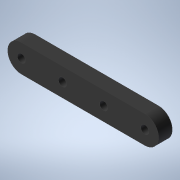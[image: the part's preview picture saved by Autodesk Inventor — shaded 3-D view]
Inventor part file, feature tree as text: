
AUTODESK INVENTOR PART (.ipt)
format: ipt  version: 2020.2 (Build 242310000, 310)  size: 146,432 bytes
history: native  units: mm
features: other x1, sketch x1, extrude x1, hole x1
ambient origin geometry x8: Origin, YZ Plane, XZ Plane, XY Plane, X Axis, Y Axis, Z Axis, Center Point
bodies: Body1 (feature_tree)
feature tree (4):
  other  "ソリッド1"
  sketch  "スケッチ1"
  extrude  "押し出し1"  Depth=10.0mm
  hole  "穴1"  [1 undecoded]
note: 1 required parameter value undecoded (feature->parameter linkage not recoverable at this tier; creation-order binding heuristic only, values carry confidence <= 0.55)
